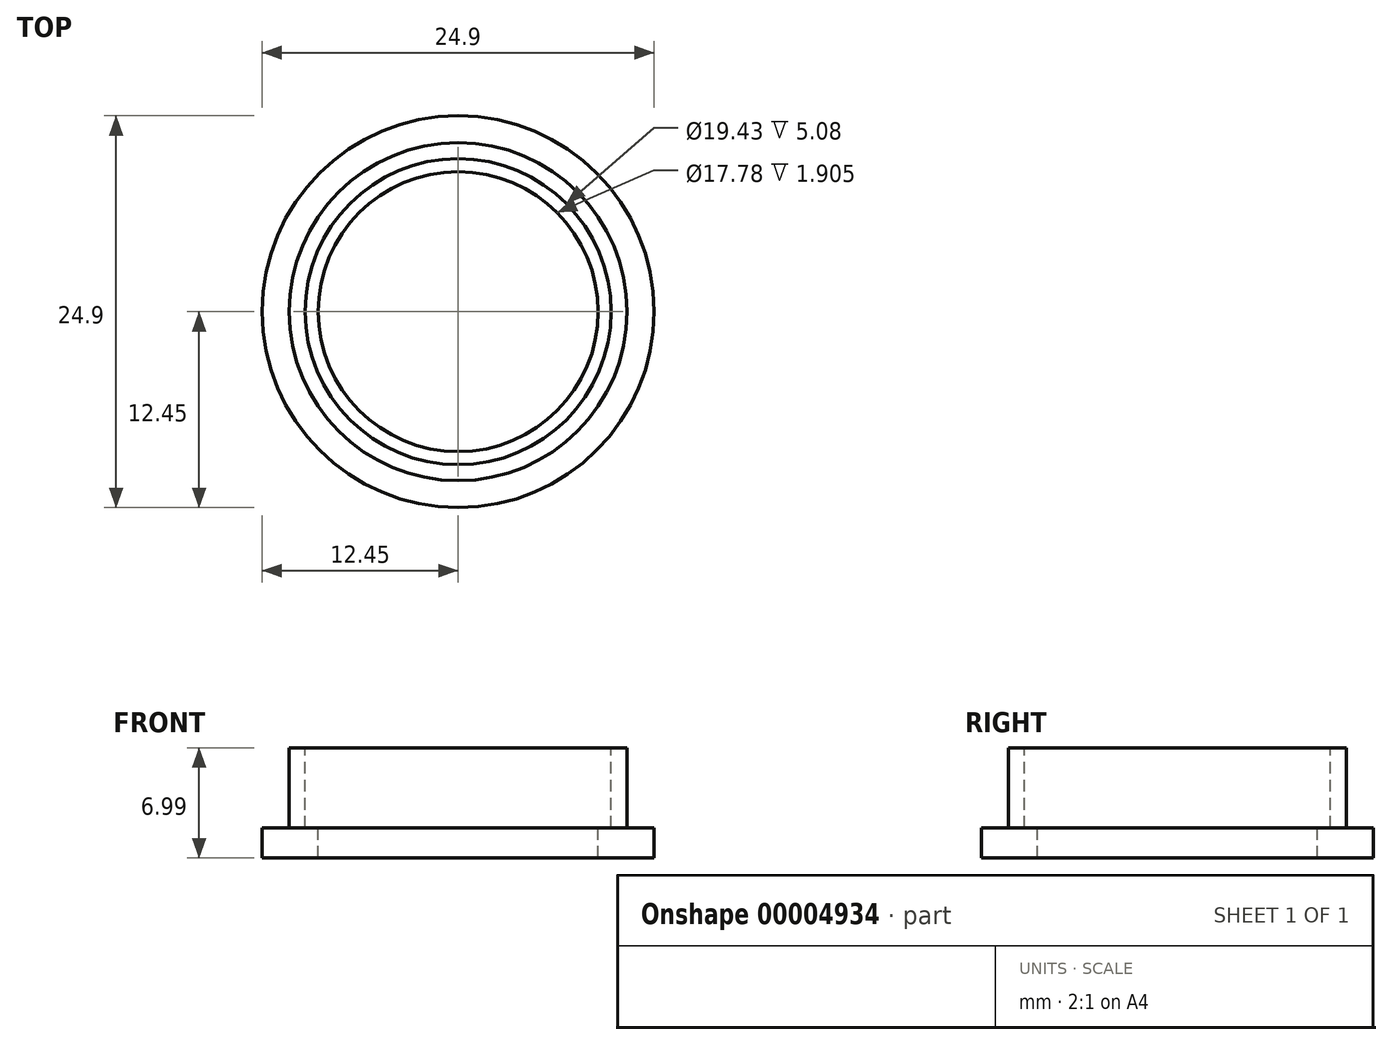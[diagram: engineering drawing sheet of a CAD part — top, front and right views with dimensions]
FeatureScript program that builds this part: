
annotation { "Feature Type Name" : "Feature", "Feature Type Description" : "" }
export const myFeature = defineFeature(function(context is Context, id is Id, definition is map)
    precondition{}
    {
        {
            var Q0;
            Q0=qCreatedBy(makeId("Top.planeOp"),FACE);
            var sketch = newSketch(context, id + "F0", { "sketchPlane" : qUnion([Q0])});
            skCircle(sketch, "E0", {"center": v(0, 0) * mm, "radius": 12.45 * mm});
            skSolve(sketch);
        }
        {
            var Q0;
            Q0=makeQuery(id+"F0.imprint","IMPRINT",FACE,{"disambiguationData":[TD([[makeQuery(id+"F0.imprint","IMPRINT",EDGE,{"derivedFrom":sQuery(id+"F0.wireOp",EDGE,"E0")}),1.0]])]});
            extrude(context, id + "F1", {"entities" : qUnion([Q0]), "depth" : 1.9 * mm});
        }
        {
            var Q0;
            Q0=makeQuery(id+"F1.opExtrude","CAP_FACE",FACE,{"disambiguationData":[OSD([sQuery(id+"F0.wireOp",EDGE,"E0")])],"isStart":false});
            var sketch = newSketch(context, id + "F2", { "sketchPlane" : qUnion([Q0])});
            skCircle(sketch, "E1", {"center": v(0, 0) * mm, "radius": 10.73 * mm});
            skSolve(sketch);
        }
        {
            var Q0;
            Q0 = qSketchRegion(id + "F2", true);
            extrude(context, id + "F3", {"entities" : qUnion([Q0]), "operationType" : NewBodyOperationType.ADD, "depth" : 5.08 * mm});
        }
        {
            var Q0;
            Q0=makeQuery(id+"F3.opExtrude","CAP_FACE",FACE,{"disambiguationData":[OSD([sQuery(id+"F2.wireOp",EDGE,"E1")])],"isStart":false});
            var sketch = newSketch(context, id + "F4", { "sketchPlane" : qUnion([Q0])});
            skCircle(sketch, "E2", {"center": v(0, 0) * mm, "radius": 9.72 * mm});
            skSolve(sketch);
        }
        {
            var Q0;
            Q0=makeQuery(id+"F4.imprint","IMPRINT",FACE,{"disambiguationData":[TD([[makeQuery(id+"F4.imprint","IMPRINT",EDGE,{"derivedFrom":sQuery(id+"F4.wireOp",EDGE,"E2")}),1.0]])]});
            var Q1;
            Q1=makeQuery(id+"F1.opExtrude","CAP_FACE",FACE,{"disambiguationData":[OSD([sQuery(id+"F0.wireOp",EDGE,"E0")])],"isStart":false});
            extrude(context, id + "F5", {"entities" : qUnion([Q0]), "operationType" : NewBodyOperationType.REMOVE, "endBound" : BoundingType.UP_TO_SURFACE, "oppositeDirection" : true, "endBoundEntityFace" : qUnion([Q1]), "depth" : 25.4 * mm});
        }
        {
            var Q0;
            Q0=makeQuery(id+"F5.boolean.opBoolean","COPY",FACE,{"derivedFrom":makeQuery(id+"F5.opExtrude","CAP_FACE",FACE,{"disambiguationData":[OSD([sQuery(id+"F4.wireOp",EDGE,"E2")])],"isStart":false})});
            var sketch = newSketch(context, id + "F6", { "sketchPlane" : qUnion([Q0])});
            skCircle(sketch, "E3", {"center": v(0, 0) * mm, "radius": 8.9 * mm});
            skSolve(sketch);
        }
        {
            var Q0;
            Q0=makeQuery(id+"F6.imprint","IMPRINT",FACE,{"disambiguationData":[TD([[makeQuery(id+"F6.imprint","IMPRINT",EDGE,{"derivedFrom":sQuery(id+"F6.wireOp",EDGE,"E3")}),1.0]])]});
            extrude(context, id + "F7", {"entities" : qUnion([Q0]), "operationType" : NewBodyOperationType.REMOVE, "endBound" : BoundingType.THROUGH_ALL, "oppositeDirection" : true, "depth" : 25.4 * mm});
        }
    });
